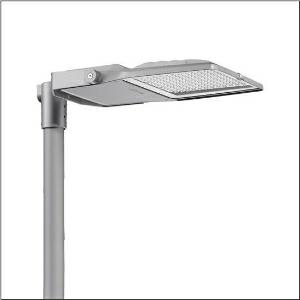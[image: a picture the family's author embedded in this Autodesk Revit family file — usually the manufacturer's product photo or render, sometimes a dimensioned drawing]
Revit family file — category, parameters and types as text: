
# Revit family: floodlight_fl_21_midi___pl61_5xa7785e2c3a_8e59
name_source: partatom
category: Lighting Fixtures
units: mm (PartAtom-declared; Revit-internal decimal feet)

## family parameters
Cut with Voids When Loaded = No
Host = Face
Light Source = No
Part Type = Normal
Room Calculation Point = No
Round Connector Dimension = Use Diameter
Shared = No

## types (1)
- --- (1 x LED, 26450 lm, 212.4 W, 3000K)
    Apparent Load = 212 VA
    CIE Flux Codes = 33 65 98 100 100
    Color Rendering = 70
    Color Temperature = 3000K
    Default Elevation = 1800 mm
    Description = Floodlight FL 21 midi, floodlight, primary light control with lens, of PMMA, primary optical cover: protective disc, of toughened safety glass, transparent, light distribution: PL61, light emission: direct distribution, installation type: surface-mounted, LED, High Power LED, rated luminous flux: 26.450lm, luminous efficacy: 125lm/W, light colour: 730, colour temperature: 3000K, control gear: Smart Interface (Zhaga), control: flexible luminous flux parameterisation, time-dependent luminous flux control, constant luminous flux control, overheat protection, pre-setting: logarithmic dimming characteristic, with terminal, 6-pole, mains connection: 220..240V, AC, 50/60Hz, start of lifetime: 212W, end of service life: 231W, reduction: 95W, luminaire housing, of diecast aluminium, powder-coated, SITECO metallic grey (DB 702S), corrosivity category C5 mid according to DIN EN ISO 12944, suitable for swimming pools, chlorine-resistant, sealing non-destructively replaceable, please order mast flange separately, mast bracket, of steel, galvanised, powder-coated, SITECO metallic grey (DB 702S), Smart Interface above, protection rating (complete): IP66, insulation class (complete): insulation class II (safety insulation), certification: CE, ENEC, VDE, protection symbol: D, impact resistance: IK08, permissible operating ambient temperature: -20..+40°C, permissible operating ambient temperature for outdoor applications: -40..+50°C, standard: DIN EN 12944, LABS conformity tested according to VDMA 24364:2018-05, packaging unit: 1 piece

Light Distribution: PL61
    Height = 76 mm
    Lamp = 1 x LED
    Lamp Light Flux = 26450 lm
    Lamp Power = 212.4 W
    Lamp count = 1
    Length = 657 mm
    Luminous efficacy = 125 lm/W
    Manufacturer = Siteco
    ModVariant = No
    Model = 5XA7785E2C3A
    Number of Poles = 1
    OnlyDefault = Yes
    Power Factor = 1
    Product Name = Floodlight FL 21 midi | PL61
    Product group = floodlight | pylon annexe
    ProductGroupID = 6201
    Protection Class = Protection class II
    Protection Degree = IP 66
    RLX_Detail_Level = 1
    RLX_Emergency_Light_Flux = 0 lm
    RLX_Emergency_Type = 0
    RLX_Emergency_Type_DB = No
    RlxData = <blob elided: 153741 chars, md5=4ecb5a13>
    Socket = socket
    Standby Power = 0 W
    System Light Flux = 26450 lm
    System Power = 212 W
    Type Comments = factory setting: luminous flux: 100 % | dim-lin: 254 | 710 mA
    Type Image = l_1007123.jpg
    URL = http://relux.com
    VarID = @adj_191617
    Voltage = 0 V
    Weight = 0.00 kg
    Width = 442 mm

## geometry (parser evidence)
native form markers: Blend x4, Sweep x12
no freeform markers — native parametric forms only
